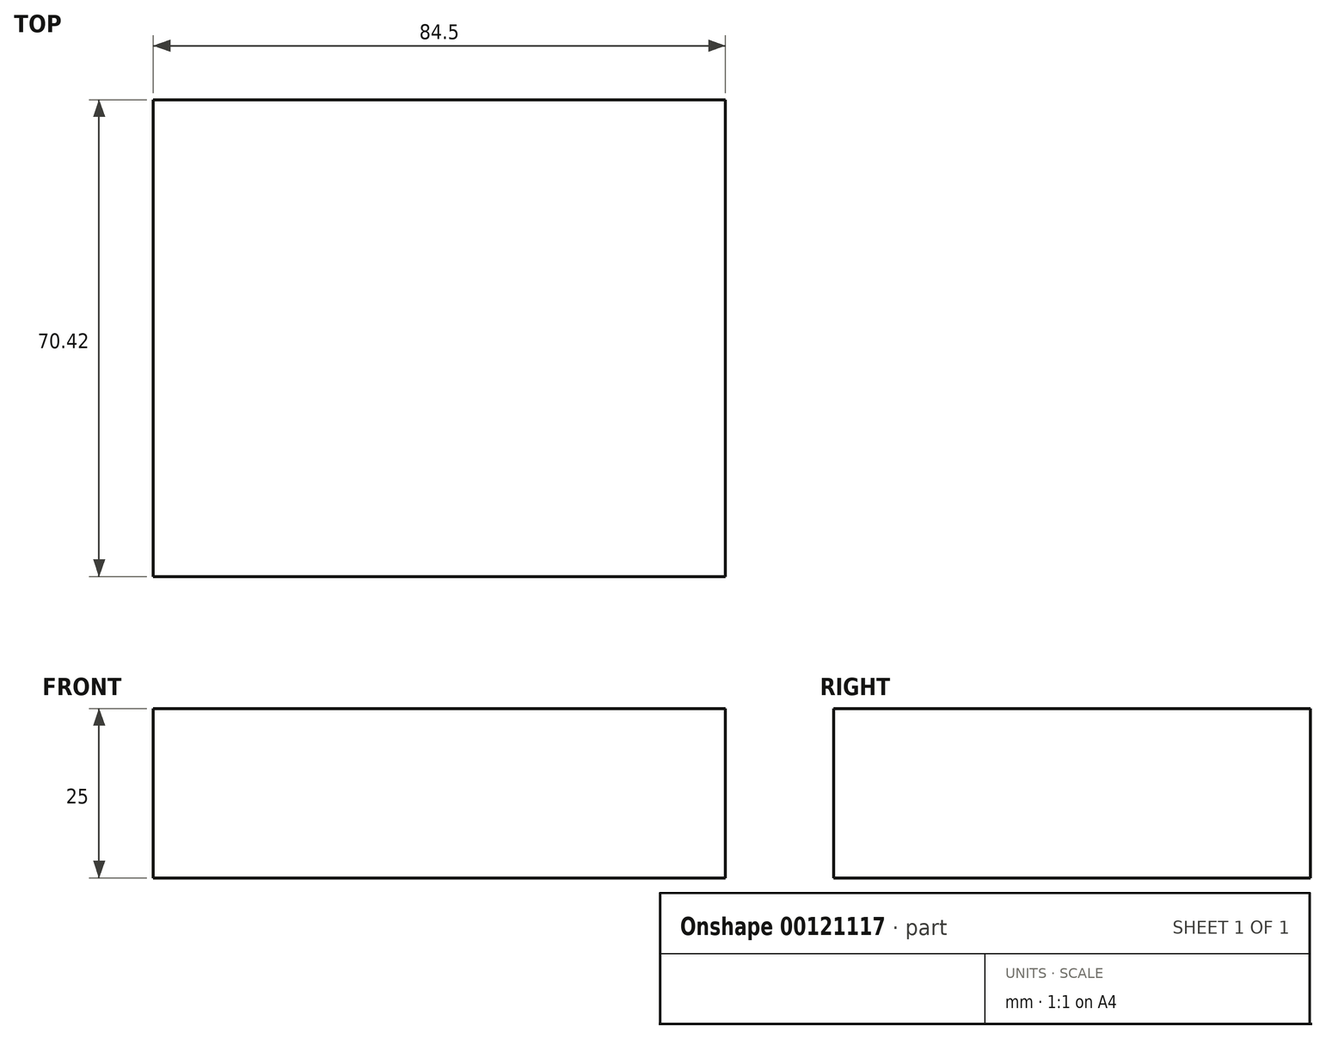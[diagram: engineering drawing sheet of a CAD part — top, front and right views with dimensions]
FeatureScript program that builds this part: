
annotation { "Feature Type Name" : "Feature", "Feature Type Description" : "" }
export const myFeature = defineFeature(function(context is Context, id is Id, definition is map)
    precondition{}
    {
        {
            var Q0;
            Q0=qCreatedBy(makeId("Top.planeOp"),FACE);
            var sketch = newSketch(context, id + "F0", { "sketchPlane" : qUnion([Q0])});
            skLineSegment(sketch, "E0.bottom", {"start": v(-84.5, -204.12) * mm, "end": v(0, -204.12) * mm});
            skLineSegment(sketch, "E0.top", {"start": v(-84.5, -164.44) * mm, "end": v(0, -164.44) * mm});
            skLineSegment(sketch, "E0.left", {"start": v(-84.5, -204.12) * mm, "end": v(-84.5, -164.44) * mm});
            skLineSegment(sketch, "E0.right", {"start": v(0, -204.12) * mm, "end": v(0, -164.44) * mm});
            skLineSegment(sketch, "E1.bottom", {"start": v(0, -164.44) * mm, "end": v(-6.93, -164.44) * mm});
            skLineSegment(sketch, "E1.top", {"start": v(0, -133.7) * mm, "end": v(-6.93, -133.7) * mm});
            skLineSegment(sketch, "E1.left", {"start": v(0, -164.44) * mm, "end": v(0, -133.7) * mm});
            skLineSegment(sketch, "E1.right", {"start": v(-6.93, -164.44) * mm, "end": v(-6.93, -133.7) * mm});
            skLineSegment(sketch, "E2.bottom", {"start": v(-6.93, -133.7) * mm, "end": v(-84.5, -133.7) * mm});
            skLineSegment(sketch, "E2.top", {"start": v(-6.93, -164.44) * mm, "end": v(-84.5, -164.44) * mm});
            skLineSegment(sketch, "E2.left", {"start": v(-6.93, -133.7) * mm, "end": v(-6.93, -164.44) * mm});
            skLineSegment(sketch, "E2.right", {"start": v(-84.5, -133.7) * mm, "end": v(-84.5, -164.44) * mm});
            skSolve(sketch);
        }
        {
            var Q0;
            Q0 = qSketchRegion(id + "F0", true);
            extrude(context, id + "F1", {"entities" : qUnion([Q0]), "depth" : 25 * mm});
        }
    });
